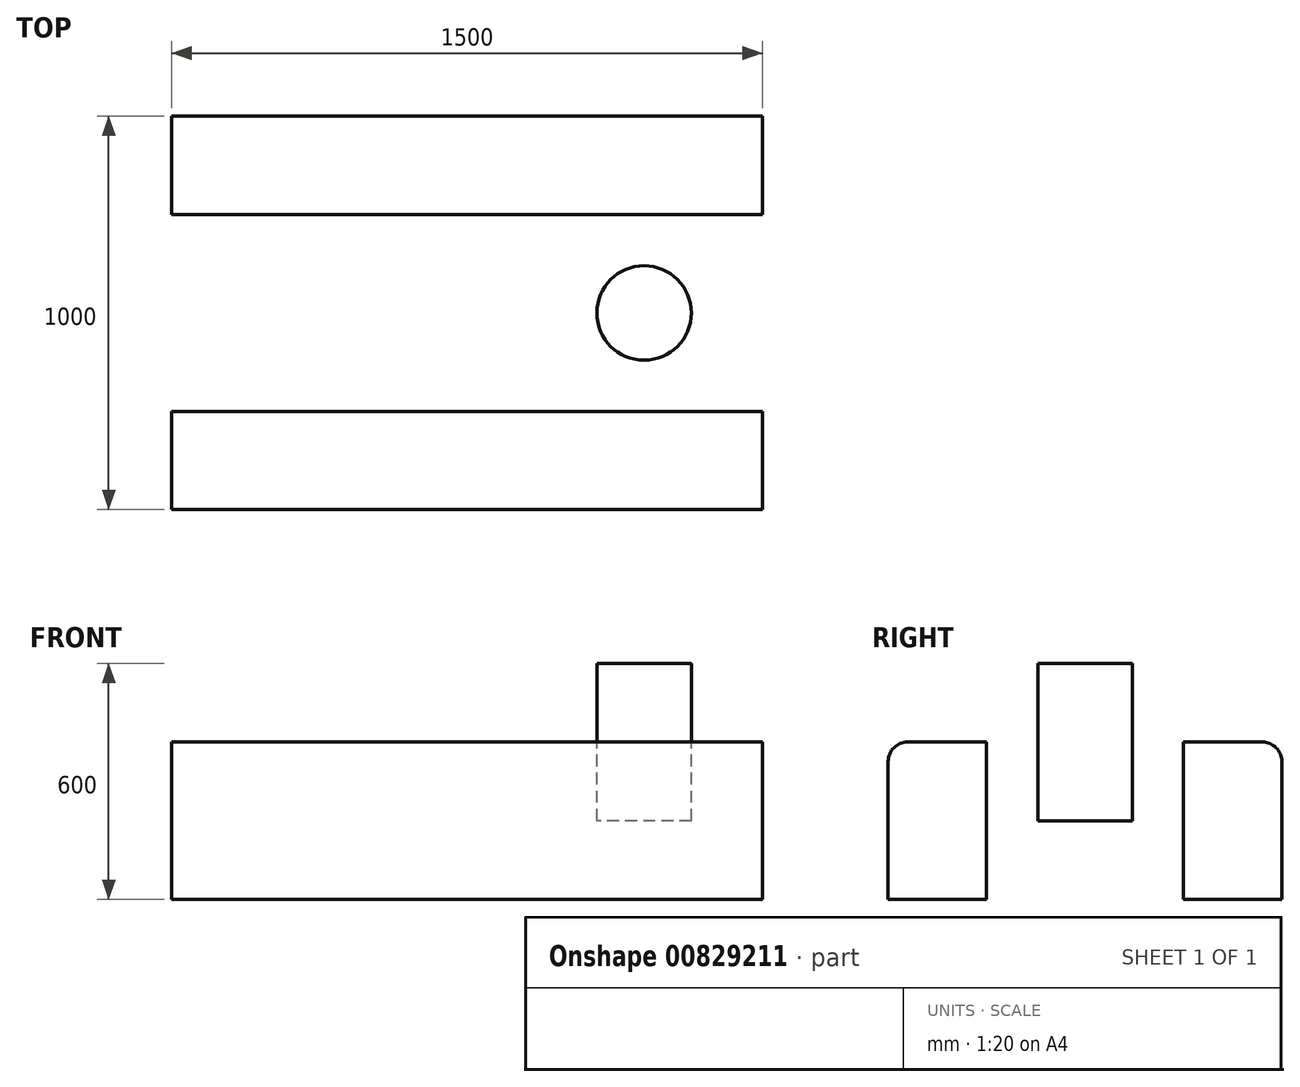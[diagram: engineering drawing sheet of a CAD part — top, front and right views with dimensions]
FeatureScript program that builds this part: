
annotation { "Feature Type Name" : "Feature", "Feature Type Description" : "" }
export const myFeature = defineFeature(function(context is Context, id is Id, definition is map)
    precondition{}
    {
        {
            var Q0;
            Q0=qCreatedBy(makeId("Right.planeOp"),FACE);
            var sketch = newSketch(context, id + "F0", { "sketchPlane" : qUnion([Q0])});
            skLineSegment(sketch, "E0", {"start": v(0, 0) * mm, "end": v(0, 724.07) * mm, "construction": true});
            skLineSegment(sketch, "E1", {"start": v(0, 724.07) * mm, "end": v(250, 724.07) * mm});
            skLineSegment(sketch, "E2", {"start": v(250, 724.07) * mm, "end": v(250, 524.07) * mm});
            skLineSegment(sketch, "E3", {"start": v(250, 524.07) * mm, "end": v(500, 524.07) * mm});
            skLineSegment(sketch, "E4", {"start": v(500, 524.07) * mm, "end": v(500, 124.07) * mm});
            skLineSegment(sketch, "E5", {"start": v(500, 124.07) * mm, "end": v(250, 124.07) * mm});
            skLineSegment(sketch, "E6", {"start": v(250, 124.07) * mm, "end": v(250, 324.07) * mm});
            skLineSegment(sketch, "E7", {"start": v(250, 324.07) * mm, "end": v(0, 324.07) * mm});
            skLineSegment(sketch, "E8.MirrorCS", {"start": v(0, 724.07) * mm, "end": v(-250, 724.07) * mm});
            skLineSegment(sketch, "E9.MirrorCS", {"start": v(-250, 724.07) * mm, "end": v(-250, 524.07) * mm});
            skLineSegment(sketch, "E10.MirrorCS", {"start": v(-250, 524.07) * mm, "end": v(-500, 524.07) * mm});
            skLineSegment(sketch, "E11.MirrorCS", {"start": v(-500, 524.07) * mm, "end": v(-500, 124.07) * mm});
            skLineSegment(sketch, "E12.MirrorCS", {"start": v(-500, 124.07) * mm, "end": v(-250, 124.07) * mm});
            skLineSegment(sketch, "E13.MirrorCS", {"start": v(-250, 124.07) * mm, "end": v(-250, 324.07) * mm});
            skLineSegment(sketch, "E14.MirrorCS", {"start": v(-250, 324.07) * mm, "end": v(0, 324.07) * mm});
            skSolve(sketch);
        }
        {
            var Q0;
            Q0=makeQuery(id+"F0.imprint","IMPRINT",FACE,{"disambiguationData":[TD([[makeQuery(id+"F0.imprint","IMPRINT",EDGE,{"derivedFrom":sQuery(id+"F0.wireOp",EDGE,"E1")}),-1.0]])]});
            extrude(context, id + "F1", {"entities" : qUnion([Q0]), "depth" : 1500 * mm, "offsetDistance" : 25 * mm});
        }
        {
            var Q0;
            Q0=makeQuery(id+"F1.opExtrude","SWEPT_FACE",FACE,{"disambiguationData":[OSD([sQuery(id+"F0.wireOp",EDGE,"E1"),sQuery(id+"F0.wireOp",EDGE,"E8.MirrorCS")])]});
            var sketch = newSketch(context, id + "F2", { "sketchPlane" : qUnion([Q0])});
            skLineSegment(sketch, "E15", {"start": v(750, 250) * mm, "end": v(750, -250) * mm, "construction": true});
            skCircle(sketch, "E16", {"center": v(300, 0) * mm, "radius": 120 * mm});
            skCircle(sketch, "E17.MirrorC", {"center": v(1200, 0) * mm, "radius": 120 * mm});
            skSolve(sketch);
        }
        {
            var Q0;
            Q0=makeQuery(id+"F2.imprint","IMPRINT",FACE,{"disambiguationData":[TD([[makeQuery(id+"F2.imprint","IMPRINT",EDGE,{"derivedFrom":sQuery(id+"F2.wireOp",EDGE,"E16")}),1.0]])]});
            var Q1;
            Q1=makeQuery(id+"F2.imprint","IMPRINT",FACE,{"disambiguationData":[TD([[makeQuery(id+"F2.imprint","IMPRINT",EDGE,{"derivedFrom":sQuery(id+"F2.wireOp",EDGE,"E17.MirrorC")}),-1.0]])]});
            var Q2;
            Q2=sQuery(id+"F2.wireOp",EDGE,"E16");
            var Q3;
            Q3=sQuery(id+"F2.wireOp",EDGE,"E17.MirrorC");
            extrude(context, id + "F3", {"entities" : qUnion([Q0, Q1]), "operationType" : NewBodyOperationType.REMOVE, "surfaceOperationType" : NewSurfaceOperationType.ADD, "surfaceEntities" : qUnion([Q2, Q3]), "oppositeDirection" : true, "depth" : 715 * mm, "offsetDistance" : 25 * mm});
        }
        {
            var Q0;
            Q0=makeQuery(id+"F1.opExtrude","SWEPT_EDGE",EDGE,{"disambiguationData":[OSD([sQuery(id+"F0.wireOp",EDGE,"E10.MirrorCS"),sQuery(id+"F0.wireOp",EDGE,"E11.MirrorCS")])]});
            var Q1;
            Q1=makeQuery(id+"F1.opExtrude","SWEPT_EDGE",EDGE,{"disambiguationData":[OSD([sQuery(id+"F0.wireOp",EDGE,"E3"),sQuery(id+"F0.wireOp",EDGE,"E4")])]});
            fillet(context, id + "F4", {"entities" : qUnion([Q0, Q1]), "radius" : 50 * mm, "tangentPropagation" : true, "allowEdgeOverflow" : false});
        }
    });
